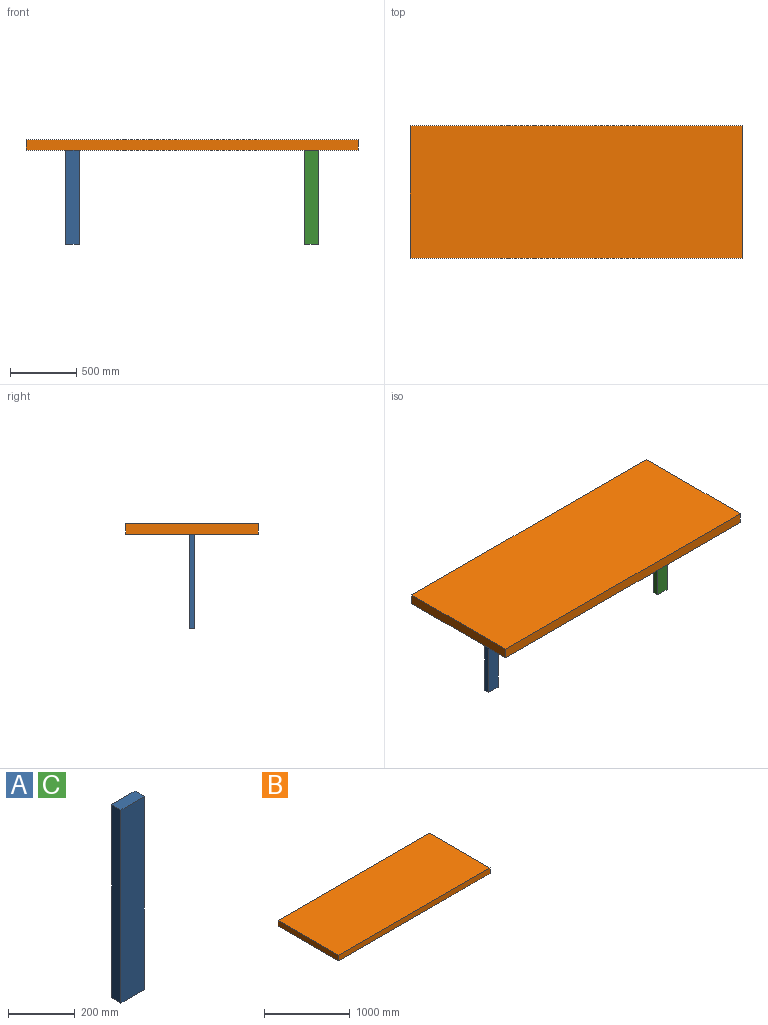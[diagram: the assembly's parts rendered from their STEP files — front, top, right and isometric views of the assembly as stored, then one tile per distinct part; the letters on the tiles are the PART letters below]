
ASSEMBLY  parts=3 mates=2
PART A: 6 faces, bbox 100x40x710 mm
  f0: plane 710x100mm, normal (0,1,0), area 71000mm2, adj f1,f2,f3,f5
  f1: plane 710x40mm, normal (1,0,0), area 28400mm2, adj f0,f3,f4,f5
  f2: plane 710x40mm, normal (-1,0,0), area 28400mm2, adj f0,f3,f4,f5
  f3: plane 100x40mm, normal (0,0,-1), area 4000mm2, adj f0,f1,f2,f4
  f4: plane 710x100mm, normal (0,-1,0), area 71000mm2, adj f1,f2,f3,f5
  f5: plane 100x40mm, normal (0,0,1), area 4000mm2, adj f0,f1,f2,f4
PART B: 6 faces, bbox 2500x1000x80 mm
  f0: plane 2500x80mm, normal (0,-1,0), area 200000mm2, adj f1,f3,f4,f5
  f1: plane 1000x80mm, normal (1,0,0), area 80000mm2, adj f0,f2,f4,f5
  f2: plane 2500x80mm, normal (0,1,0), area 200000mm2, adj f1,f3,f4,f5
  f3: plane 1000x80mm, normal (-1,0,0), area 80000mm2, adj f0,f2,f4,f5
  f4: plane 2500x1000mm, normal (0,0,1), area 2500000mm2, adj f0,f1,f2,f3
  f5: plane 2500x1000mm, normal (0,0,-1), area 2500000mm2, adj f0,f1,f2,f3
PART C: same geometry as A
PLACE A t=(-958,-295,-393)mm
PLACE B rot(axis=(1,0,0),180deg) t=(-8,85,42)mm
PLACE C t=(842,-295,-393)mm
MATE fastened C.f5 <-> B.f4  axis (0,0,1) through (892,85,-38)mm
MATE fastened A.f5 <-> B.f4  axis (0,0,1) through (-908,85,-38)mm
